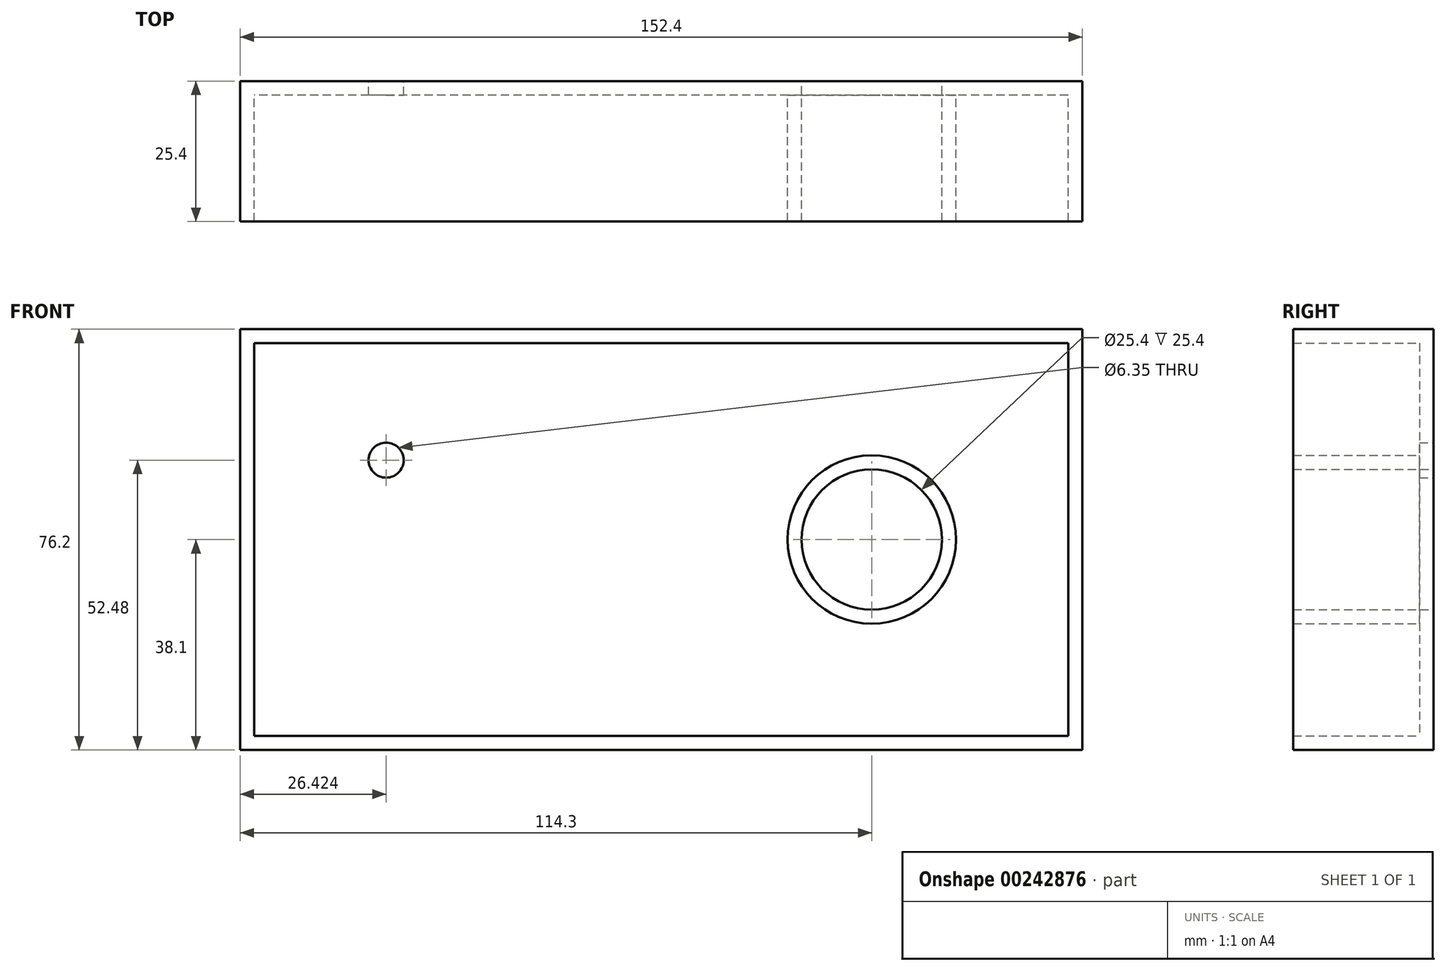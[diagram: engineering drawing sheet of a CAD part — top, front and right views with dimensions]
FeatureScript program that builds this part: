
annotation { "Feature Type Name" : "Feature", "Feature Type Description" : "" }
export const myFeature = defineFeature(function(context is Context, id is Id, definition is map)
    precondition{}
    {
        {
            var Q0;
            Q0=qCreatedBy(makeId("Front.planeOp"),FACE);
            var sketch = newSketch(context, id + "F0", { "sketchPlane" : qUnion([Q0])});
            skLineSegment(sketch, "E0.bottom", {"start": v(76.2, 38.1) * mm, "end": v(-76.2, 38.1) * mm});
            skLineSegment(sketch, "E0.top", {"start": v(76.2, -38.1) * mm, "end": v(-76.2, -38.1) * mm});
            skLineSegment(sketch, "E0.left", {"start": v(76.2, 38.1) * mm, "end": v(76.2, -38.1) * mm});
            skLineSegment(sketch, "E0.right", {"start": v(-76.2, 38.1) * mm, "end": v(-76.2, -38.1) * mm});
            skPoint(sketch, "E0.middle", {"position": v(0, 0) * mm});
            skCircle(sketch, "E1", {"center": v(38.1, 0) * mm, "radius": 12.7 * mm});
            skSolve(sketch);
        }
        {
            var Q0;
            Q0=makeQuery(id+"F0.imprint","IMPRINT",FACE,{"disambiguationData":[TD([[makeQuery(id+"F0.imprint","IMPRINT",EDGE,{"derivedFrom":sQuery(id+"F0.wireOp",EDGE,"E0.bottom")}),1.0]])]});
            extrude(context, id + "F1", {"entities" : qUnion([Q0]), "depth" : 25.4 * mm});
        }
        {
            var Q0;
            Q0=makeQuery(id+"F1.opExtrude","CAP_FACE",FACE,{"disambiguationData":[OSD([sQuery(id+"F0.wireOp",EDGE,"E0.bottom"),sQuery(id+"F0.wireOp",EDGE,"E0.top"),sQuery(id+"F0.wireOp",EDGE,"E0.left"),sQuery(id+"F0.wireOp",EDGE,"E0.right"),sQuery(id+"F0.wireOp",EDGE,"E1")])],"isStart":false});
            shell(context, id + "F2", {"entities" : qUnion([Q0]), "thickness" : 2.54 * mm});
        }
        {
            var Q0;
            Q0=qCreatedBy(makeId("Front.planeOp"),FACE);
            var sketch = newSketch(context, id + "F3", { "sketchPlane" : qUnion([Q0])});
            skEllipse(sketch, "E2", {"center": v(-49.78, 14.38) * mm, "majorRadius": 16.03 * mm, "minorRadius": 4.43 * mm, "majorAxis": v(-0.3, -0.95)});
            skSolve(sketch);
        }
        {
            var Q0;
            Q0=sQuery(id+"F3.wireOp",VERTEX,"E2.center");
            var Q1;
            Q1=makeQuery(id+"F1.opExtrude","SWEPT_BODY",BODY,{"disambiguationData":[OSD([sQuery(id+"F0.wireOp",EDGE,"E0.bottom"),sQuery(id+"F0.wireOp",EDGE,"E0.top"),sQuery(id+"F0.wireOp",EDGE,"E0.left"),sQuery(id+"F0.wireOp",EDGE,"E0.right"),sQuery(id+"F0.wireOp",EDGE,"E1")])]});
            hole(context, id + "F4", {"style" : HoleStyle.SIMPLE, "endStyle" : HoleEndStyle.THROUGH, "oppositeDirection" : true, "holeDiameter" : 6.35 * mm, "tappedDepth" : 12.7 * mm, "tapClearance" : 3, "locations" : qUnion([Q0]), "scope" : qUnion([Q1])});
        }
    });
